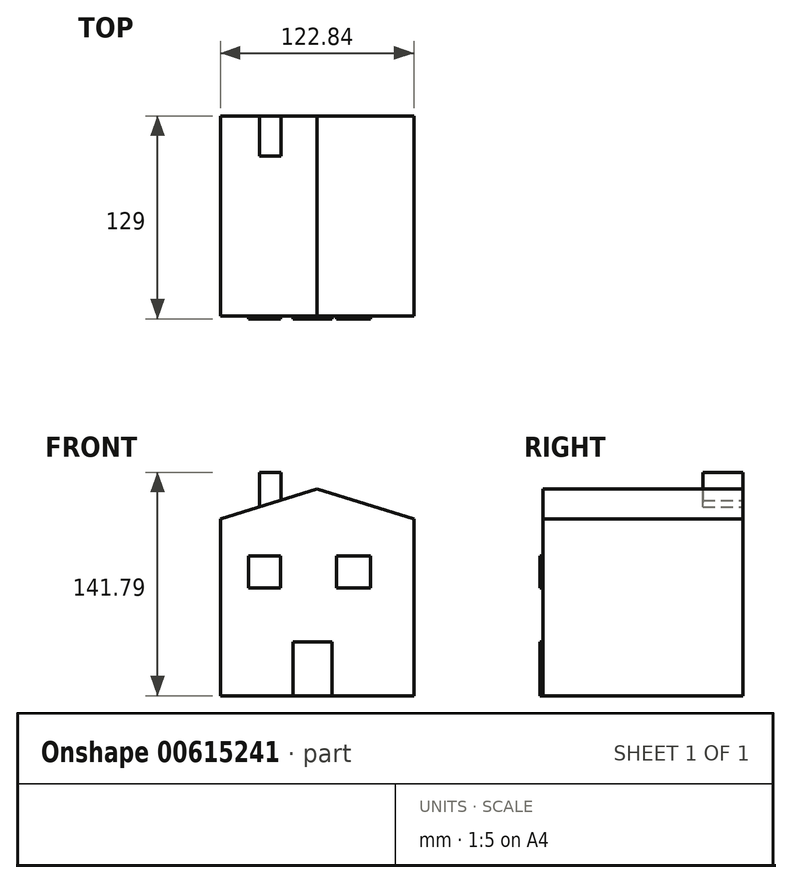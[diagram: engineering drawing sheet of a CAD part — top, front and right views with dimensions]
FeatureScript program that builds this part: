
annotation { "Feature Type Name" : "Feature", "Feature Type Description" : "" }
export const myFeature = defineFeature(function(context is Context, id is Id, definition is map)
    precondition{}
    {
        {
            var Q0;
            Q0=qCreatedBy(makeId("Front.planeOp"),FACE);
            var sketch = newSketch(context, id + "F0", { "sketchPlane" : qUnion([Q0])});
            skLineSegment(sketch, "E0.bottom", {"start": v(61.42, 56.05) * mm, "end": v(-61.42, 56.05) * mm});
            skLineSegment(sketch, "E0.top", {"start": v(61.42, -56.05) * mm, "end": v(-61.42, -56.05) * mm});
            skLineSegment(sketch, "E0.left", {"start": v(61.42, 56.05) * mm, "end": v(61.42, -56.05) * mm});
            skLineSegment(sketch, "E0.right", {"start": v(-61.42, 56.05) * mm, "end": v(-61.42, -56.05) * mm});
            skPoint(sketch, "E0.middle", {"position": v(0, 0) * mm});
            skLineSegment(sketch, "E1", {"start": v(-61.42, 56.05) * mm, "end": v(0, 75.1) * mm});
            skLineSegment(sketch, "E2", {"start": v(0, 75.1) * mm, "end": v(61.42, 56.05) * mm});
            skLineSegment(sketch, "E3", {"start": v(-23.03, 67.96) * mm, "end": v(-23.03, 85.74) * mm});
            skLineSegment(sketch, "E4", {"start": v(-23.03, 85.74) * mm, "end": v(-36.6, 85.74) * mm});
            skLineSegment(sketch, "E5", {"start": v(-36.6, 85.74) * mm, "end": v(-36.6, 63.75) * mm});
            skSolve(sketch);
        }
        {
            var Q0;
            Q0=makeQuery(id+"F0.imprint","IMPRINT",FACE,{"disambiguationData":[TD([[makeQuery(id+"F0.imprint","IMPRINT",EDGE,{"derivedFrom":sQuery(id+"F0.wireOp",EDGE,"E0.bottom")}),1.0]])]});
            var Q1;
            {var subQ3=sQuery(id+"F0.wireOp",EDGE,"E0.bottom");Q1=makeQuery(id+"F0.imprint","IMPRINT",FACE,{"disambiguationData":[TD([[makeQuery(id+"F0.imprint","IMPRINT",EDGE,{"derivedFrom":subQ3}),-1.0]])]});}
            extrude(context, id + "F1", {"entities" : qUnion([Q0, Q1]), "depth" : 127 * mm, "offsetDistance" : 25.4 * mm});
        }
        {
            var Q0;
            {var subQ0=sQuery(id+"F0.wireOp",EDGE,"E3");Q0=makeQuery(id+"F0.imprint","IMPRINT",FACE,{"disambiguationData":[TD([[makeQuery(id+"F0.imprint","IMPRINT",EDGE,{"derivedFrom":subQ0}),1.0]])]});}
            extrude(context, id + "F2", {"entities" : qUnion([Q0]), "operationType" : NewBodyOperationType.ADD, "depth" : 25.4 * mm, "offsetDistance" : 25.4 * mm});
        }
        {
            var Q0;
            Q0=makeQuery(id+"F1.opExtrude","CAP_FACE",FACE,{"disambiguationData":[OSD([sQuery(id+"F0.wireOp",EDGE,"E0.top"),sQuery(id+"F0.wireOp",EDGE,"E0.left"),sQuery(id+"F0.wireOp",EDGE,"E0.right"),sQuery(id+"F0.wireOp",EDGE,"E1"),sQuery(id+"F0.wireOp",EDGE,"E2")])],"isStart":false});
            var sketch = newSketch(context, id + "F3", { "sketchPlane" : qUnion([Q0])});
            skLineSegment(sketch, "E6", {"start": v(-15.41, -56.05) * mm, "end": v(-15.41, -22) * mm});
            skLineSegment(sketch, "E7", {"start": v(-15.41, -22) * mm, "end": v(9.57, -22) * mm});
            skLineSegment(sketch, "E8", {"start": v(9.57, -22) * mm, "end": v(9.57, -56.05) * mm});
            skSolve(sketch);
        }
        {
            var Q0;
            {var subQ0=sQuery(id+"F3.wireOp",EDGE,"E6");Q0=makeQuery(id+"F3.imprint","IMPRINT",FACE,{"disambiguationData":[TD([[makeQuery(id+"F3.imprint","IMPRINT",EDGE,{"derivedFrom":subQ0}),-1.0]])]});}
            extrude(context, id + "F4", {"entities" : qUnion([Q0]), "operationType" : NewBodyOperationType.ADD, "depth" : 2 * mm, "offsetDistance" : 25.4 * mm});
        }
        {
            var Q0;
            Q0=makeQuery(id+"F1.opExtrude","CAP_FACE",FACE,{"disambiguationData":[OSD([sQuery(id+"F0.wireOp",EDGE,"E0.top"),sQuery(id+"F0.wireOp",EDGE,"E0.left"),sQuery(id+"F0.wireOp",EDGE,"E0.right"),sQuery(id+"F0.wireOp",EDGE,"E1"),sQuery(id+"F0.wireOp",EDGE,"E2")])],"isStart":false});
            var sketch = newSketch(context, id + "F5", { "sketchPlane" : qUnion([Q0])});
            skLineSegment(sketch, "E9", {"start": v(-43.65, 32.84) * mm, "end": v(-23.2, 32.84) * mm});
            skLineSegment(sketch, "E10", {"start": v(-23.2, 32.84) * mm, "end": v(-23.2, 12.4) * mm});
            skLineSegment(sketch, "E11", {"start": v(-23.2, 12.4) * mm, "end": v(-43.65, 12.4) * mm});
            skLineSegment(sketch, "E12", {"start": v(-43.65, 12.4) * mm, "end": v(-43.65, 32.84) * mm});
            skLineSegment(sketch, "E13", {"start": v(-33.42, 32.84) * mm, "end": v(-33.42, 12.4) * mm});
            skLineSegment(sketch, "E14", {"start": v(-43.65, 22.62) * mm, "end": v(-23.2, 22.62) * mm});
            skLineSegment(sketch, "E15.bottom", {"start": v(12.25, 32.84) * mm, "end": v(33.72, 32.84) * mm});
            skLineSegment(sketch, "E15.top", {"start": v(12.25, 12.4) * mm, "end": v(33.72, 12.4) * mm});
            skLineSegment(sketch, "E15.left", {"start": v(12.25, 32.84) * mm, "end": v(12.25, 12.4) * mm});
            skLineSegment(sketch, "E15.right", {"start": v(33.72, 32.84) * mm, "end": v(33.72, 12.4) * mm});
            skPoint(sketch, "E15.middle", {"position": v(22.98, 22.62) * mm});
            skPoint(sketch, "E15.middle.positionSnap0", {"position": v(-33.42, 22.62) * mm});
            skPoint(sketch, "E15.centerSnap0", {"position": v(-33.42, 22.62) * mm});
            skSolve(sketch);
        }
        {
            var Q0;
            Q0 = qSketchRegion(id + "F5", true);
            extrude(context, id + "F6", {"entities" : qUnion([Q0]), "operationType" : NewBodyOperationType.ADD, "depth" : 2 * mm, "offsetDistance" : 25.4 * mm});
        }
    });
